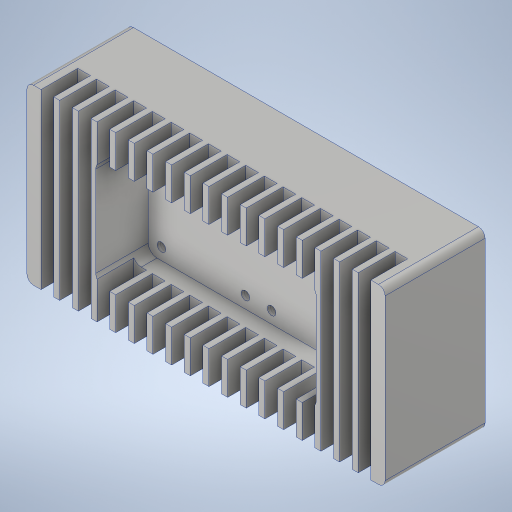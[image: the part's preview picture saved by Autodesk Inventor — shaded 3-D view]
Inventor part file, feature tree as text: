
AUTODESK INVENTOR PART (.ipt)
format: ipt  version: 2023.4 (Build 274418000, 418)  size: 454,144 bytes
history: native  units: in
note: dims shown in document units (in); Inventor stores cm internally (conversion verified against a paired STEP export)
features: sketch x5, extrude x4, fillet x2, pattern_linear x1, hole x1, projected_geometry x1
ambient origin geometry x8: Origin, YZ Plane, XZ Plane, XY Plane, X Axis, Y Axis, Z Axis, Center Point
bodies: Solid1 (feature_tree)
feature tree (14):
  extrude  "Extrusion1"  Depth=2.6in
  extrude  "Extrusion2"  Depth=3.3071in
  fillet  "Fillet1"  Radius=1.6142in
  sketch  "Sketch4"  dims[d6=0.7874in d7=0.0in d8=0.13in]
  sketch  "Sketch5"  dims[d20=0.212in]
  extrude  "Extrusion3"  Depth=0.13in
  pattern_linear  "Rectangular Pattern1"  Spacing1=0.5512in  [1 undecoded]
  fillet  "Fillet2"  Radius=0.28in
  extrude  "Extrusion4"  Depth=0.1in
  hole  "Hole2"  [1 undecoded]
  sketch  "Sketch1"  dims[d0=5.375in d1=2.6in]
  sketch  "Sketch2"  dims[d2=1.5in d3=0.0in d4=3.3071in d5=1.6142in]
  projected_geometry  "Projected Loop1"
  sketch  "Sketch7"  dims[d21=0.19in d22=0.5512in d23=0.0in d24=7.0866in d26=0.28in d27=0.1in d29=4.675in d30=2.2in d31=2.6in d32=0.2in d33=5.375in d34=0.35in d35=0.13in d36=0.3in d37=0.0in d42=1.2598in d43=1.2598in d44=1.2598in d45=1.2598in d46=0.1969in d47=1.6142in d48=0.1772in d49=0.13in d50=0.328in d51=0.375in d52=0.25in d53=0.5635in d54=1.0in d55=0.8108in]
note: 2 required parameter values undecoded (feature->parameter linkage not recoverable at this tier; creation-order binding heuristic only, values carry confidence <= 0.55)
